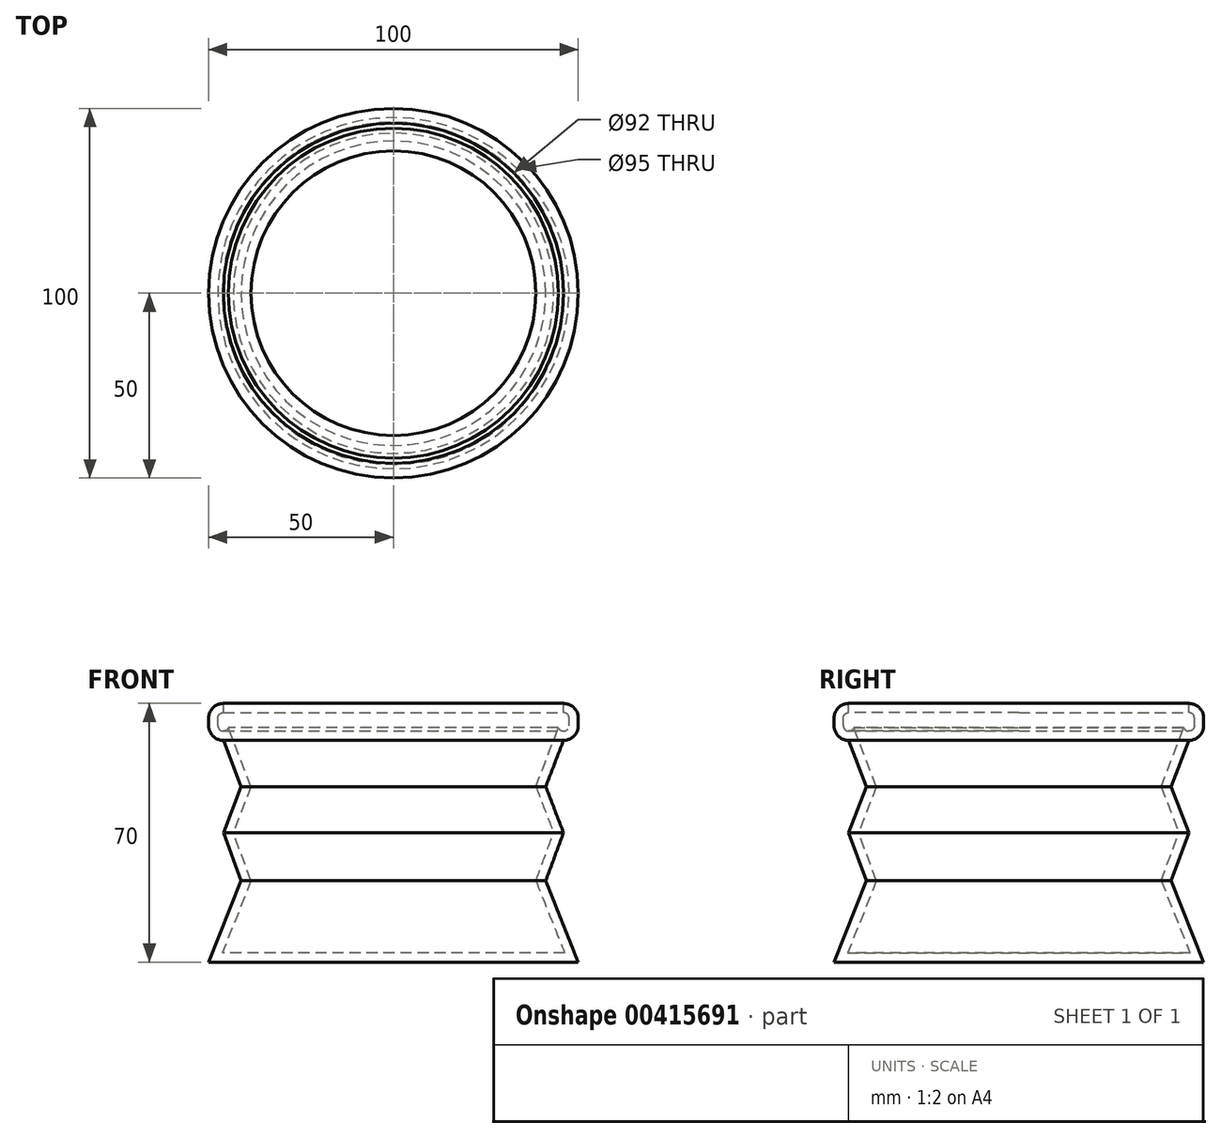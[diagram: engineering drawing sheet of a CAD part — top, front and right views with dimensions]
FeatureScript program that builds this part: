
annotation { "Feature Type Name" : "Feature", "Feature Type Description" : "" }
export const myFeature = defineFeature(function(context is Context, id is Id, definition is map)
    precondition{}
    {
        {
            var Q0;
            Q0=qCreatedBy(makeId("Front.planeOp"),FACE);
            var sketch = newSketch(context, id + "F0", { "sketchPlane" : qUnion([Q0])});
            skLineSegment(sketch, "E0.bottom", {"start": v(0, -35) * mm, "end": v(-50, -35) * mm});
            skLineSegment(sketch, "E0.top", {"start": v(0, 35) * mm, "end": v(-46, 35) * mm});
            skLineSegment(sketch, "E0.right", {"start": v(-50, 29) * mm, "end": v(-50, 31) * mm});
            skPoint(sketch, "E0.middle", {"position": v(0, 0) * mm});
            skPoint(sketch, "E1.visualSharp", {"position": v(-50, 35) * mm});
            skArc(sketch, "E1.filletArc", {"start": v(-46, 35) * mm, "mid": v(-48.83, 33.83) * mm, "end": v(-50, 31) * mm});
            skLineSegment(sketch, "E2", {"start": v(0, 25) * mm, "end": v(-46, 25) * mm});
            skArc(sketch, "E3.filletArc", {"start": v(-50, 29) * mm, "mid": v(-48.83, 26.17) * mm, "end": v(-46, 25) * mm});
            skLineSegment(sketch, "E4", {"start": v(-46, 25) * mm, "end": v(-46, -25) * mm, "construction": true});
            skLineSegment(sketch, "E5", {"start": v(-46, -25) * mm, "end": v(-50, -35) * mm});
            skLineSegment(sketch, "E6", {"start": v(-46, -12.97) * mm, "end": v(0, -12.97) * mm, "construction": true});
            skLineSegment(sketch, "E7", {"start": v(-46, 25) * mm, "end": v(-41.19, 12.5) * mm});
            skLineSegment(sketch, "E8", {"start": v(-41.19, 12.5) * mm, "end": v(-46, 0) * mm});
            skLineSegment(sketch, "E9", {"start": v(-46, 0) * mm, "end": v(-41.19, -12.97) * mm});
            skLineSegment(sketch, "E10", {"start": v(-41.19, -12.97) * mm, "end": v(-46, -25) * mm});
            skLineSegment(sketch, "E11", {"start": v(0, 35) * mm, "end": v(0, -35) * mm});
            skPoint(sketch, "E11.endSnap0", {"position": v(0, -35) * mm});
            skLineSegment(sketch, "E12.trimOffspring", {"start": v(0, 0) * mm, "end": v(-50, 0) * mm, "construction": true});
            skLineSegment(sketch, "E13.trimOffspring", {"start": v(0, 12.5) * mm, "end": v(-50, 12.5) * mm, "construction": true});
            skSolve(sketch);
        }
        {
            var Q0;
            Q0=qCreatedBy(makeId("Top.planeOp"),FACE);
            var sketch = newSketch(context, id + "F1", { "sketchPlane" : qUnion([Q0])});
            skCircle(sketch, "E14", {"center": v(0, 0) * mm, "radius": 15.72 * mm});
            skSolve(sketch);
        }
        {
            var Q0;
            Q0=makeQuery(id+"F1.imprint","IMPRINT",FACE,{"disambiguationData":[TD([[makeQuery(id+"F1.imprint","IMPRINT",EDGE,{"derivedFrom":sQuery(id+"F1.wireOp",EDGE,"E14")}),1.0]])]});
            extrude(context, id + "F2", {"entities" : qUnion([Q0]), "endBound" : BoundingType.SYMMETRIC, "depth" : 70 * mm});
        }
        {
            var Q0;
            {var subQ1=sQuery(id+"F0.wireOp",EDGE,"E0.bottom");Q0=makeQuery(id+"F0.imprint","IMPRINT",FACE,{"disambiguationData":[TD([[makeQuery(id+"F0.imprint","IMPRINT",EDGE,{"derivedFrom":subQ1}),-1.0]])]});}
            var Q1;
            {var subQ1=sQuery(id+"F0.wireOp",EDGE,"E0.top");Q1=makeQuery(id+"F0.imprint","IMPRINT",FACE,{"disambiguationData":[TD([[makeQuery(id+"F0.imprint","IMPRINT",EDGE,{"derivedFrom":subQ1}),1.0]])]});}
            var Q2;
            Q2=sQuery(id+"F0.wireOp",EDGE,"E11");
            revolve(context, id + "F3", {"operationType" : NewBodyOperationType.ADD, "entities" : qUnion([Q0, Q1]), "axis" : qUnion([Q2]), "revolveType" : RevolveType.FULL});
        }
        {
            var Q0;
            Q0=makeQuery(id+"F3.boolean.opBoolean","MERGE",FACE,{"derivedFrom":[makeQuery(id+"F2.opExtrude","CAP_FACE",FACE,{"disambiguationData":[OSD([sQuery(id+"F1.wireOp",EDGE,"E14")])],"isStart":false}),makeQuery(id+"F3.opRevolve","SWEPT_FACE",FACE,{"disambiguationData":[OSD([sQuery(id+"F0.wireOp",EDGE,"E0.top")])]})]});
            shell(context, id + "F4", {"entities" : qUnion([Q0]), "thickness" : 2.5 * mm});
        }
    });
